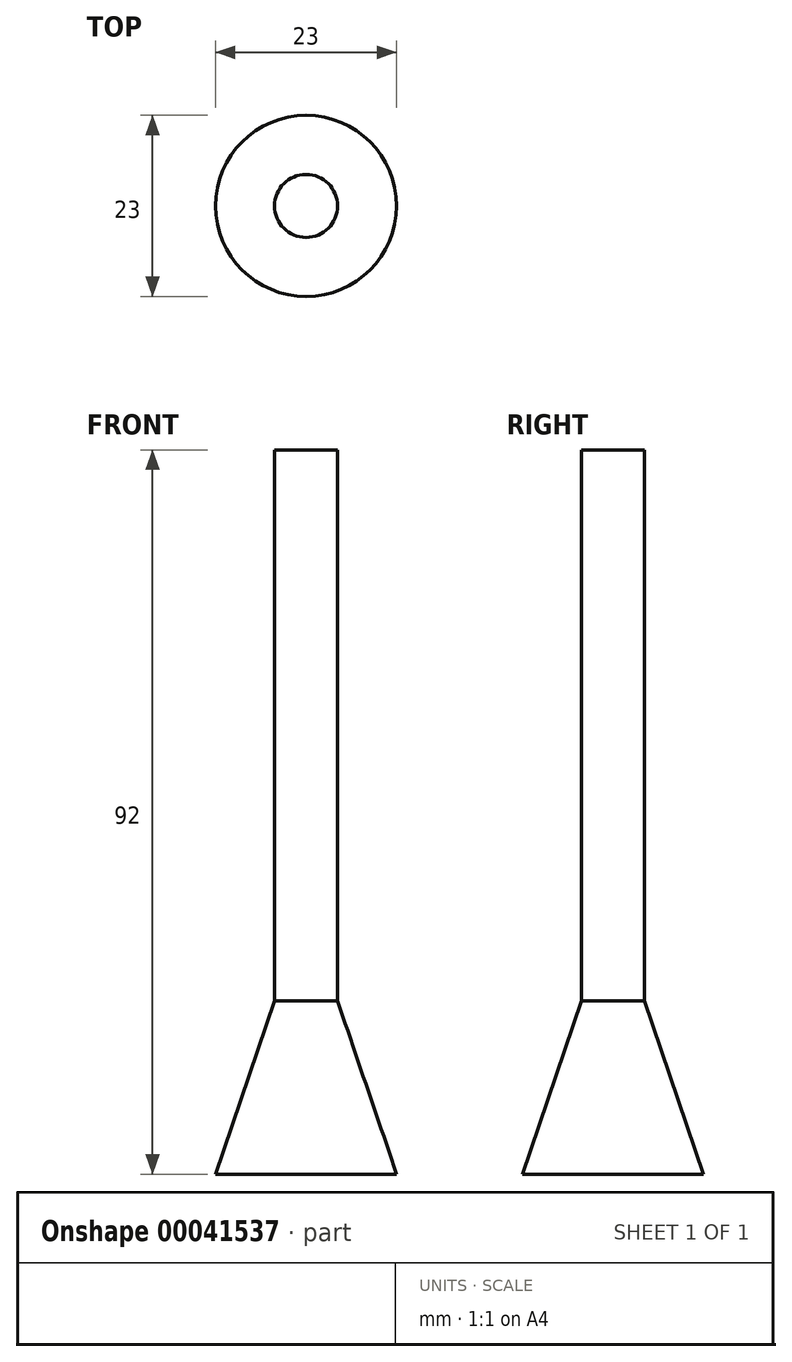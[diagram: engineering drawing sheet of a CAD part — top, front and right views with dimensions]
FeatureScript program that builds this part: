
annotation { "Feature Type Name" : "Feature", "Feature Type Description" : "" }
export const myFeature = defineFeature(function(context is Context, id is Id, definition is map)
    precondition{}
    {
        {
            var Q0;
            Q0=qCreatedBy(makeId("Top.planeOp"),FACE);
            var sketch = newSketch(context, id + "F0", { "sketchPlane" : qUnion([Q0])});
            skCircle(sketch, "E0", {"center": v(0, 0) * mm, "radius": 11.5 * mm});
            skSolve(sketch);
        }
        {
            var Q0;
            Q0=qCreatedBy(makeId("Top.planeOp"),FACE);
            cPlane(context, id + "F1", {"entities" : qUnion([Q0]), "cplaneType" : CPlaneType.OFFSET, "offset" : 22 * mm, "width" : 150 * mm, "height" : 150 * mm});
        }
        {
            var Q0;
            Q0=qCreatedBy(id+"F1.planeOp",FACE);
            var sketch = newSketch(context, id + "F2", { "sketchPlane" : qUnion([Q0])});
            skPoint(sketch, "E1.0", {"position": v(0, 0) * mm});
            skCircle(sketch, "E2", {"center": v(0, 0) * mm, "radius": 4 * mm});
            skSolve(sketch);
        }
        {
            var Q0;
            Q0=makeQuery(id+"F0.imprint","IMPRINT",FACE,{"disambiguationData":[TD([[makeQuery(id+"F0.imprint","IMPRINT",EDGE,{"derivedFrom":sQuery(id+"F0.wireOp",EDGE,"E0")}),1.0]])]});
            var Q1;
            Q1=makeQuery(id+"F2.imprint","IMPRINT",FACE,{"disambiguationData":[TD([[makeQuery(id+"F2.imprint","IMPRINT",EDGE,{"derivedFrom":sQuery(id+"F2.wireOp",EDGE,"E2")}),1.0]])]});
            loft(context, id + "F3", {"sheetProfilesArray" : [{ "sheetProfileEntities" : qUnion([Q0]) }, { "sheetProfileEntities" : qUnion([Q1]) }]});
        }
        {
            var Q0;
            Q0=makeQuery(id+"F3.opLoft","CAP_FACE",FACE,{"disambiguationData":[OSD([makeQuery(id+"F2.imprint","IMPRINT",FACE,{"disambiguationData":[TD([[makeQuery(id+"F2.imprint","IMPRINT",EDGE,{"derivedFrom":sQuery(id+"F2.wireOp",EDGE,"E2")}),1.0]])]})])],"isStart":true});
            extrude(context, id + "F4", {"entities" : qUnion([Q0]), "operationType" : NewBodyOperationType.ADD, "depth" : 70 * mm});
        }
    });
